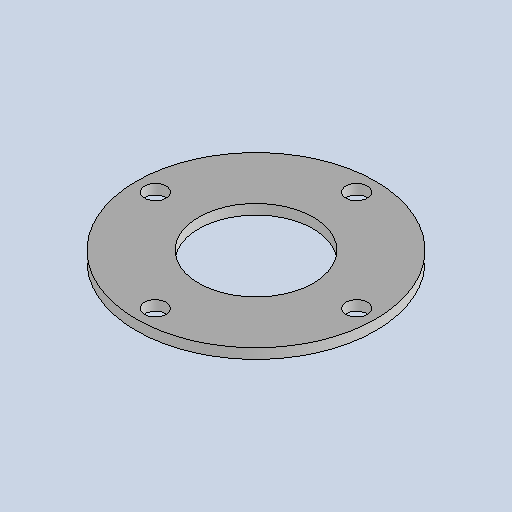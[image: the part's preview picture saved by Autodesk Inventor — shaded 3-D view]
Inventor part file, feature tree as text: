
AUTODESK INVENTOR PART (.ipt)
format: ipt  version: 2025.1 (Build 291241020, 241B)  size: 145,920 bytes
history: native  units: mm
features: other x3, sketch x2, sheet_metal_op x1, pattern_circular x1
ambient origin geometry x8: Origin, YZ Plane, XZ Plane, XY Plane, X Axis, Y Axis, Z Axis, Center Point
bodies: Body1 (feature_tree)
feature tree (7):
  sheet_metal_op  "Face2"
  pattern_circular  "Circular Pattern1"  [2 undecoded]
  sketch  "Sketch2"  dims[d14=8.0mm]
  other  "Plate2"
  sketch  "Sketch3"  dims[d15=17.0mm d17=8.0mm d18=0.0mm d19=40.0mm d20=360.0deg d25=91.0mm d27=190.0mm d28=160.0mm]
  other  "Cut1"
  other  "Definition1"
note: 2 required parameter values undecoded (feature->parameter linkage not recoverable at this tier; creation-order binding heuristic only, values carry confidence <= 0.55)
